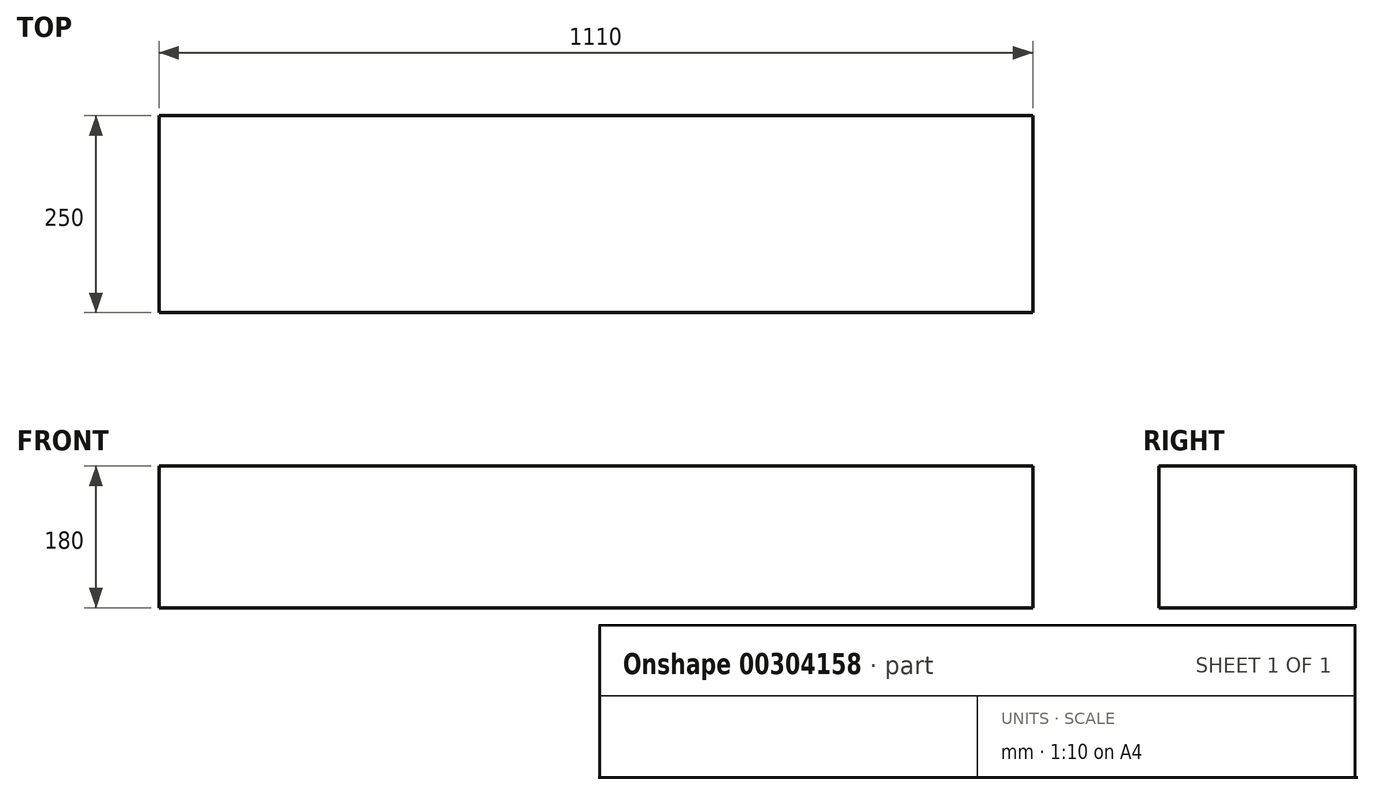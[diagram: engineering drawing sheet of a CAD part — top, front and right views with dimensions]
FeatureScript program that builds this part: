
annotation { "Feature Type Name" : "Feature", "Feature Type Description" : "" }
export const myFeature = defineFeature(function(context is Context, id is Id, definition is map)
    precondition{}
    {
        {
            var Q0;
            Q0=qCreatedBy(makeId("Top.planeOp"),FACE);
            var sketch = newSketch(context, id + "F0", { "sketchPlane" : qUnion([Q0])});
            skLineSegment(sketch, "E0.bottom", {"start": v(-559.3, -3.5) * mm, "end": v(550.7, -3.5) * mm});
            skLineSegment(sketch, "E0.top", {"start": v(-559.3, -253.5) * mm, "end": v(550.7, -253.5) * mm});
            skLineSegment(sketch, "E0.left", {"start": v(-559.3, -3.5) * mm, "end": v(-559.3, -253.5) * mm});
            skLineSegment(sketch, "E0.right", {"start": v(550.7, -3.5) * mm, "end": v(550.7, -253.5) * mm});
            skSolve(sketch);
        }
        {
            var Q0;
            Q0=makeQuery(id+"F0.imprint","IMPRINT",FACE,{"disambiguationData":[TD([[makeQuery(id+"F0.imprint","IMPRINT",EDGE,{"derivedFrom":sQuery(id+"F0.wireOp",EDGE,"E0.bottom")}),-1.0]])]});
            extrude(context, id + "F1", {"entities" : qUnion([Q0]), "depth" : 180 * mm});
        }
    });
